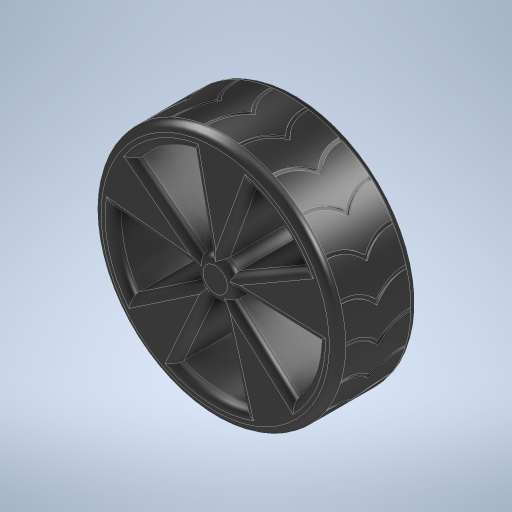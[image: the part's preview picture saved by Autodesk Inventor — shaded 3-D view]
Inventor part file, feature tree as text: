
AUTODESK INVENTOR PART (.ipt)
format: ipt  version: 2023 (Build 270158000, 158)  size: 822,272 bytes
history: native  units: in
note: dims shown in document units (in); Inventor stores cm internally (conversion verified against a paired STEP export)
features: extrude x3, sketch x3, fillet x2, pattern_circular x2, plane x1, projected_geometry x1
ambient origin geometry x8: Origin, YZ Plane, XZ Plane, XY Plane, X Axis, Y Axis, Z Axis, Center Point
bodies: Solid1 (feature_tree)
feature tree (12):
  extrude  "Extrusion1"  Depth=0.7874in TaperAngle=0.0deg
  fillet  "Fillet1"  Radius=0.0787in
  extrude  "Extrusion2"  Depth=0.3937in
  pattern_circular  "Circular Pattern1"  [2 undecoded]
  fillet  "Fillet2"  Radius=1.9685in
  plane  "Work Plane1"
  extrude  "Extrusion3"  Depth=0.3937in
  pattern_circular  "Circular Pattern2"  Count=3  [1 undecoded]
  sketch  "Sketch2"  dims[d0=2.3622in d1=0.7874in d2=0.0in d3=0.0787in]
  sketch  "Sketch3"  dims[d4=0.3937in d5=1.9685in]
  sketch  "Sketch4"  dims[d6=30.0deg d7=0.3937in d8=0.0in d9=1.9685in d10=360.0deg d12=0.0787in d13=1.1811in d17=0.0197in d18=0.0in d19=8.6614in d20=360.0deg]
  projected_geometry  "Projected Loop1"
note: 3 required parameter values undecoded (feature->parameter linkage not recoverable at this tier; creation-order binding heuristic only, values carry confidence <= 0.55)
